# Revit family: Haworth_Belong_Cubby
name_source: partatom
category: Furniture Systems
revit_build: Autodesk Revit 2018 (Build: 20170223_1515(x64)
units: mm (PartAtom-declared; Revit-internal decimal feet)

## family parameters
Always vertical = Yes
Cut with Voids When Loaded = No
OmniClass Number = 23.40.70.14.64.21
OmniClass Title = Systems Furniture
Part Type = Normal
Room Calculation Point = No
Round Connector Dimension = Use Diameter
Shared = No
Work Plane-Based = No

## types (3) — shared parameters
Actual Depth = 10"
Actual Width = 15"
Assembly Code = E2020200
Custom Size = Yes
Description = Haworth - Belong - Cubby
Manufacturer = Haworth
Max. Width = 15"
Metal Depth = 1/16"
Min. Width = 15"
Model = Haworth - Belong - Cubby
Product Page URL = http://www.haworth.com
Revision Number = 2
Size = Verify Final Dim. w/ Haworth
Slat Gap = 1 169/256"
Slat Height = 87/256"
Slat Offset = 1 7/32"
Slat Top Offset = 1 53/64"
Standard 12in = No
Standard 8in = No
Standard Depth = 10 in.
Standard Heights = 9, 12 in.
Standard Width = 15 in.
Sustainability Info = https://www.haworth.com
Trim Finish = Haworth _ Paint _ Putty
URL = www.haworth.com
Warranty = http://www.haworth.com
Width = 15"

## per-type parameters (varying)
| type | 12in Cubby Height | 9in Cubby Height | Actual Height |
| 12h - With Slots | Yes | No | 12" |
| 12h - No Slots | Yes | No | 12" |
| 9h - No Slots | No | Yes | 9" |

## geometry (parser evidence)
native form markers: Sweep x3
no freeform markers — native parametric forms only
